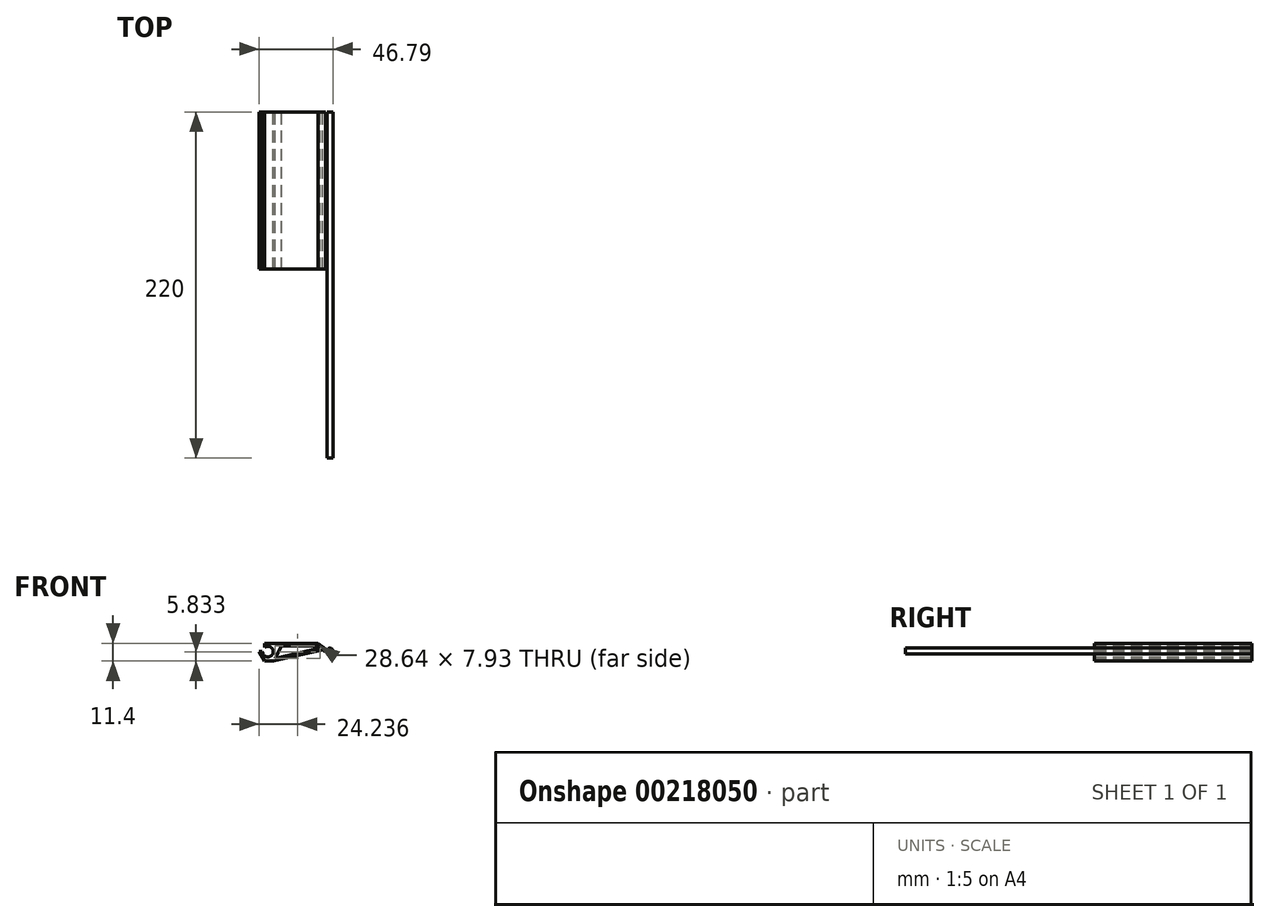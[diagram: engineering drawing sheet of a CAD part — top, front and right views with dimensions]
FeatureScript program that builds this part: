
annotation { "Feature Type Name" : "Feature", "Feature Type Description" : "" }
export const myFeature = defineFeature(function(context is Context, id is Id, definition is map)
    precondition{}
    {
        {
            var Q0;
            Q0=qCreatedBy(makeId("Front.planeOp"),FACE);
            var sketch = newSketch(context, id + "F0", { "sketchPlane" : qUnion([Q0])});
            skArc(sketch, "E0", {"start": v(36.87, 2.02) * mm, "mid": v(40.61, -2.5) * mm, "end": v(39.82, 3.32) * mm});
            skLineSegment(sketch, "E1", {"start": v(39.39, 3.81) * mm, "end": v(39.39, 3.82) * mm});
            skPoint(sketch, "E2.endSnap0", {"position": v(39.39, 4.35) * mm});
            skLineSegment(sketch, "E3", {"start": v(31.94, 5.35) * mm, "end": v(9.39, 5.35) * mm});
            skPoint(sketch, "E4.orphan", {"position": v(37.79, 4.35) * mm});
            skLineSegment(sketch, "E5", {"start": v(8.55, 3.75) * mm, "end": v(3.44, -6.05) * mm});
            skLineSegment(sketch, "E6", {"start": v(3.44, -6.05) * mm, "end": v(-2.16, -6.05) * mm});
            skLineSegment(sketch, "E7", {"start": v(-2.16, -6.05) * mm, "end": v(-5.5, 0) * mm});
            skLineSegment(sketch, "E8", {"start": v(-5.5, 0) * mm, "end": v(-3.82, 0) * mm});
            skLineSegment(sketch, "E9", {"start": v(0, 3.35) * mm, "end": v(0, 5.35) * mm});
            skLineSegment(sketch, "E10", {"start": v(0, 5.35) * mm, "end": v(9.39, 5.35) * mm});
            skLineSegment(sketch, "E11", {"start": v(33.97, 3.75) * mm, "end": v(8.55, 3.75) * mm});
            skPoint(sketch, "E12.visualSharp", {"position": v(-5.5, 0) * mm});
            skPoint(sketch, "E13.visualSharp", {"position": v(-3.35, 0) * mm});
            skPoint(sketch, "E14.visualSharp", {"position": v(-2.16, -6.05) * mm});
            skPoint(sketch, "E15.visualSharp", {"position": v(3.44, -6.05) * mm});
            skPoint(sketch, "E16.visualSharp", {"position": v(8.55, 3.75) * mm});
            skPoint(sketch, "E17.visualSharp", {"position": v(0, 3.35) * mm});
            skPoint(sketch, "E18.visualSharp", {"position": v(0, 5.35) * mm});
            skPoint(sketch, "E19.visualSharp", {"position": v(39.39, 5.35) * mm});
            skPoint(sketch, "E20.visualSharp", {"position": v(37.79, 3.75) * mm});
            skPoint(sketch, "E21.visualSharp", {"position": v(37.79, 2.9) * mm});
            skPoint(sketch, "E22.visualSharp", {"position": v(39.39, 3.35) * mm});
            skLineSegment(sketch, "E23", {"start": v(0, 3.35) * mm, "end": v(62.82, 3.35) * mm, "construction": true});
            skLineSegment(sketch, "E24.trimOffspring", {"start": v(39.39, 4.33) * mm, "end": v(39.39, 4.35) * mm});
            skPoint(sketch, "E25.visualSharp", {"position": v(38.71, 5.35) * mm});
            skArc(sketch, "E26.trimOffspring", {"start": v(39.39, 3.35) * mm, "mid": v(39.6, 3.34) * mm, "end": v(39.82, 3.32) * mm});
            skPoint(sketch, "E27.visualSharp", {"position": v(36.3, 3.75) * mm});
            skArc(sketch, "E28.trimOffspring", {"start": v(38.12, 3.08) * mm, "mid": v(38.74, 3.28) * mm, "end": v(39.39, 3.35) * mm});
            skLineSegment(sketch, "E29", {"start": v(36.64, 1.64) * mm, "end": v(31.94, 5.35) * mm});
            skLineSegment(sketch, "E30.0", {"start": v(36.38, -0.2) * mm, "end": v(31.38, 3.75) * mm});
            skArc(sketch, "E31", {"start": v(38.12, 3.08) * mm, "mid": v(37.42, 2.64) * mm, "end": v(36.87, 2.02) * mm});
            skCircle(sketch, "E32", {"center": v(39.39, 0.3) * mm, "radius": 2 * mm});
            skCircle(sketch, "E33", {"center": v(39.39, 0.3) * mm, "radius": 1.9 * mm});
            skArc(sketch, "E34.converted", {"start": v(-2.94, -1.61) * mm, "mid": v(2.88, -1.7) * mm, "end": v(0, 3.35) * mm});
            skLineSegment(sketch, "E35", {"start": v(3.44, -6.05) * mm, "end": v(34.67, 1.16) * mm});
            skLineSegment(sketch, "E36.0", {"start": v(4.42, -4.18) * mm, "end": v(33.06, 2.43) * mm});
            skLineSegment(sketch, "E37", {"start": v(-3.82, 0) * mm, "end": v(-2.94, -1.61) * mm});
            skArc(sketch, "E38", {"start": v(0, 3.35) * mm, "mid": v(-1.05, 3.18) * mm, "end": v(-2, 2.69) * mm});
            skLineSegment(sketch, "E39", {"start": v(-2, 2.69) * mm, "end": v(-2, 5.35) * mm});
            skLineSegment(sketch, "E40", {"start": v(-2, 5.35) * mm, "end": v(0, 5.35) * mm});
            skSolve(sketch);
        }
        {
            var Q0;
            Q0=makeQuery(id+"F0.imprint","IMPRINT",FACE,{"disambiguationData":[TD([[makeQuery(id+"F0.imprint","IMPRINT",EDGE,{"derivedFrom":sQuery(id+"F0.wireOp",EDGE,"Kf3w7t7D-FLBp-rtQi-3koo-v1eVYvvDfHh4")}),-1.0]])]});
            var Q1;
            {var subQ4=sQuery(id+"F0.wireOp",EDGE,"rvePJwIH-3ANZ-lDGn-Q9o7-DrdEnluy2YEu");Q1=makeQuery(id+"F0.imprint","IMPRINT",FACE,{"disambiguationData":[TD([[makeQuery(id+"F0.imprint","IMPRINT",EDGE,{"derivedFrom":subQ4}),-1.0]])]});}
            var Q2;
            {var subQ0=sQuery(id+"F0.wireOp",EDGE,"SHBwMagn-x46g-bAgj-vJCy-rmVyF4jb0zbE");Q2=makeQuery(id+"F0.imprint","IMPRINT",FACE,{"disambiguationData":[TD([[makeQuery(id+"F0.imprint","IMPRINT",EDGE,{"derivedFrom":subQ0}),-1.0]])]});}
            var Q3;
            Q3=makeQuery(id+"F0.imprint","IMPRINT",FACE,{"disambiguationData":[TD([[makeQuery(id+"F0.imprint","IMPRINT",EDGE,{"derivedFrom":sQuery(id+"F0.wireOp",EDGE,"E3")}),1.0]])]});
            var Q4;
            {var subQ3=sQuery(id+"F0.wireOp",EDGE,"E30.0");Q4=makeQuery(id+"F0.imprint","IMPRINT",FACE,{"disambiguationData":[TD([[makeQuery(id+"F0.imprint","IMPRINT",EDGE,{"derivedFrom":subQ3}),-1.0]])]});}
            var Q5;
            {var subQ0=sQuery(id+"F0.wireOp",EDGE,"E26.trimOffspring");Q5=makeQuery(id+"F0.imprint","IMPRINT",FACE,{"disambiguationData":[TD([[makeQuery(id+"F0.imprint","IMPRINT",EDGE,{"derivedFrom":subQ0}),-1.0]])]});}
            var Q6;
            {var subQ0=sQuery(id+"F0.wireOp",EDGE,"fuJJtQWe-kVRp-GaWU-bn1f-3bUKWTy8wSQN");Q6=makeQuery(id+"F0.imprint","IMPRINT",FACE,{"disambiguationData":[TD([[makeQuery(id+"F0.imprint","IMPRINT",EDGE,{"derivedFrom":subQ0}),1.0]])]});}
            var Q7;
            {var subQ0=sQuery(id+"F0.wireOp",EDGE,"eX7EJS0L-YHCd-stIE-RDSr-YGeIrVrZMk0z");Q7=makeQuery(id+"F0.imprint","IMPRINT",FACE,{"disambiguationData":[TD([[makeQuery(id+"F0.imprint","IMPRINT",EDGE,{"derivedFrom":subQ0}),1.0]])]});}
            var Q8;
            {var subQ0=sQuery(id+"F0.wireOp",EDGE,"E35");Q8=makeQuery(id+"F0.imprint","IMPRINT",FACE,{"disambiguationData":[TD([[makeQuery(id+"F0.imprint","IMPRINT",EDGE,{"derivedFrom":subQ0}),1.0]])]});}
            var Q9;
            Q9=makeQuery(id+"F0.imprint","IMPRINT",FACE,{"disambiguationData":[TD([[makeQuery(id+"F0.imprint","IMPRINT",EDGE,{"derivedFrom":sQuery(id+"F0.wireOp",EDGE,"E9")}),1.0]])]});
            extrude(context, id + "F1", {"entities" : qUnion([Q0, Q1, Q2, Q3, Q4, Q5, Q6, Q7, Q8, Q9]), "depth" : 100 * mm});
        }
        {
            var Q0;
            Q0=makeQuery(id+"F0.imprint","IMPRINT",FACE,{"disambiguationData":[TD([[makeQuery(id+"F0.imprint","IMPRINT",EDGE,{"derivedFrom":sQuery(id+"F0.wireOp",EDGE,"E33")}),1.0]])]});
            extrude(context, id + "F2", {"entities" : qUnion([Q0]), "depth" : 220 * mm});
        }
    });
